# Revit family: AMZ 113_DN15-32_RFA
name_source: partatom
category: Pipe Accessories
units: mm (PartAtom-declared; Revit-internal decimal feet)

## family parameters
Always vertical = Yes
Cut with Voids When Loaded = No
OmniClass Number = 23.65.55.14.17
OmniClass Title = Adjusting/Controlling Valves for Liquid Services
Part Type = Valve - Breaks Into
Round Connector Dimension = Use Diameter
Shared = No
Work Plane-Based = No

## types (8) — shared parameters
082G1637 = AMZ Actuator_RFA : AMZ 112/113 Actuator_24V_082G1637
082G1638 = AMZ Actuator_RFA : AMZ 112/113 Actuator_230V_082G1638
Connection = Internal thread
Description = Motorized Control Valve
IfcExportAs = IfcValveType
IfcExportType = AMZ 113
LOD 200 = No
LOD 350 = Yes
Manufacturer = Danfoss
Max Medium Temperature = 130 °C
Max Operating Pressure = 6 bar
Min Medium Temperature = 2 °C
Nominal Flow (Text) = PN 40
Power = 4 VA
Power Consumption = 3.5 VA
URL = https://store.danfoss.com
Valve Body Material = Danfoss Copper Alloy

## per-type parameters (varying)
- AMZ 113_DN15_230V_082G5418: AMZ Actuator=AMZ Actuator_RFA : AMZ 112/113 Actuator_230V_082G1638; D=15 mm  [stored 0.0492126 ft]; H1=38 mm; H2=29 mm  [stored 0.0951444 ft]; HS=9 mm  [stored 0.0295276 ft]; Kvs=4.3 m³/h; L1=3.5 mm  [stored 0.0114829 ft]; LS=37 mm; Length=64.5 mm; Model=082G5418; Model Type=AMZ 113_DN15_230V; Power Supply=230 VAC; R1=11 mm  [stored 0.0360892 ft]; RN1=13.53 mm; RV1=13.53 mm; RV2=17 mm  [stored 0.0557743 ft]; RV3=9.06 mm; Voltage=230 V; W1=26.4 mm  [stored 0.0866142 ft]; W2=13.2 mm  [stored 0.0433071 ft]; W3=3.5 mm  [stored 0.0114829 ft]; W4=4 mm  [stored 0.0131234 ft]; WS1=18.5 mm  [stored 0.0606955 ft]; WS2=-18.5 mm  [stored -0.0606955 ft]; Weight=1.16 kg; connector diameter=27.06 mm; nut_depth1=5.75 mm  [stored 0.0188648 ft]; nut_depth2=6 mm  [stored 0.019685 ft]; nut_length=27.1 mm  [stored 0.0889108 ft]
- AMZ 113_DN20_230V_082G5419: AMZ Actuator=AMZ Actuator_RFA : AMZ 112/113 Actuator_230V_082G1638; D=20 mm  [stored 0.0656168 ft]; H1=42 mm; H2=33 mm; HS=9 mm  [stored 0.0295276 ft]; Kvs=8.3 m³/h; L1=3 mm  [stored 0.00984252 ft]; LS=37 mm; Length=76 mm; Model=082G5419; Model Type=AMZ 113_DN20_230V; Power Supply=230 VAC; R1=11 mm  [stored 0.0360892 ft]; RN1=17 mm  [stored 0.0557743 ft]; RV1=17.2 mm  [stored 0.0564304 ft]; RV2=21 mm  [stored 0.0688976 ft]; RV3=9.06 mm; Voltage=230 V; W1=28.5 mm  [stored 0.0935039 ft]; W2=17.2 mm  [stored 0.0564304 ft]; W3=3.5 mm  [stored 0.0114829 ft]; W4=4 mm  [stored 0.0131234 ft]; WS1=18.6 mm  [stored 0.0610236 ft]; WS2=-18.6 mm  [stored -0.0610236 ft]; Weight=1.42 kg; connector diameter=34 mm; nut_depth1=9.5 mm  [stored 0.031168 ft]; nut_depth2=9.5 mm  [stored 0.031168 ft]; nut_length=34 mm
- AMZ 113_DN25_230V_082G5420: AMZ Actuator=AMZ Actuator_RFA : AMZ 112/113 Actuator_230V_082G1638; D=25 mm  [stored 0.082021 ft]; H1=47 mm; H2=37.5 mm; HS=9.5 mm  [stored 0.031168 ft]; Kvs=13.0 m³/h; L1=3 mm  [stored 0.00984252 ft]; LS=42 mm; Length=97 mm; Model=082G5420; Model Type=AMZ 113_DN25_230V; Power Supply=230 VAC; R1=11.5 mm  [stored 0.0377297 ft]; RN1=22.19 mm; RV1=23 mm  [stored 0.0754593 ft]; RV2=26 mm; RV3=14 mm  [stored 0.0459318 ft]; Voltage=230 V; W1=35.5 mm; W2=20.1 mm  [stored 0.0659449 ft]; W3=3 mm  [stored 0.00984252 ft]; W4=6 mm  [stored 0.019685 ft]; WS1=21 mm  [stored 0.0688976 ft]; WS2=-21 mm  [stored -0.0688976 ft]; Weight=1.91 kg; connector diameter=44.38 mm; nut_depth1=12 mm  [stored 0.0393701 ft]; nut_depth2=12.5 mm  [stored 0.0410105 ft]; nut_length=44.38 mm
- AMZ 113_DN32_230V_082G5421: AMZ Actuator=AMZ Actuator_RFA : AMZ 112/113 Actuator_230V_082G1638; D=32 mm; H1=61.25 mm; H2=51.25 mm; HS=10 mm  [stored 0.0328084 ft]; Kvs=21.0 m³/h; L1=3 mm  [stored 0.00984252 ft]; LS=42 mm; Length=118 mm; Model=082G5421; Model Type=AMZ 113_DN32_230V; Power Supply=230 VAC; R1=11.5 mm  [stored 0.0377297 ft]; RN1=30 mm  [stored 0.0984252 ft]; RV1=28 mm  [stored 0.0918635 ft]; RV2=31 mm; RV3=15 mm  [stored 0.0492126 ft]; Voltage=230 V; W1=48 mm; W2=23.5 mm  [stored 0.0770997 ft]; W3=3 mm  [stored 0.00984252 ft]; W4=7.6 mm; WS1=21 mm  [stored 0.0688976 ft]; WS2=-21 mm  [stored -0.0688976 ft]; Weight=3.71 kg; connector diameter=60 mm; nut_depth1=11 mm  [stored 0.0360892 ft]; nut_depth2=11 mm  [stored 0.0360892 ft]; nut_length=60 mm
- AMZ 113_DN15_24V_082G5412: AMZ Actuator=AMZ Actuator_RFA : AMZ 112/113 Actuator_24V_082G1637; D=15 mm  [stored 0.0492126 ft]; H1=38 mm; H2=29 mm  [stored 0.0951444 ft]; HS=9 mm  [stored 0.0295276 ft]; Kvs=4.3 m³/h; L1=3.5 mm  [stored 0.0114829 ft]; LS=37 mm; Length=64.5 mm; Model=082G5412; Model Type=AMZ 113_DN15_24V; Power Supply=24 VAC; R1=11 mm  [stored 0.0360892 ft]; RN1=13.53 mm; RV1=13.53 mm; RV2=17 mm  [stored 0.0557743 ft]; RV3=9.06 mm; Voltage=24 V; W1=26.4 mm  [stored 0.0866142 ft]; W2=13.2 mm  [stored 0.0433071 ft]; W3=3.5 mm  [stored 0.0114829 ft]; W4=4 mm  [stored 0.0131234 ft]; WS1=18.5 mm  [stored 0.0606955 ft]; WS2=-18.5 mm  [stored -0.0606955 ft]; Weight=1.16 kg; connector diameter=27.06 mm; nut_depth1=5.75 mm  [stored 0.0188648 ft]; nut_depth2=6 mm  [stored 0.019685 ft]; nut_length=27.1 mm  [stored 0.0889108 ft]
- AMZ 113_DN20_24V_082G5413: AMZ Actuator=AMZ Actuator_RFA : AMZ 112/113 Actuator_24V_082G1637; D=20 mm  [stored 0.0656168 ft]; H1=42 mm; H2=33 mm; HS=9 mm  [stored 0.0295276 ft]; Kvs=8.3 m³/h; L1=3 mm  [stored 0.00984252 ft]; LS=37 mm; Length=76 mm; Model=082G5413; Model Type=AMZ 113_DN20_24V; Power Supply=24 VAC; R1=11 mm  [stored 0.0360892 ft]; RN1=17 mm  [stored 0.0557743 ft]; RV1=17.2 mm  [stored 0.0564304 ft]; RV2=21 mm  [stored 0.0688976 ft]; RV3=9.06 mm; Voltage=24 V; W1=28.5 mm  [stored 0.0935039 ft]; W2=17.2 mm  [stored 0.0564304 ft]; W3=3.5 mm  [stored 0.0114829 ft]; W4=4 mm  [stored 0.0131234 ft]; WS1=18.6 mm  [stored 0.0610236 ft]; WS2=-18.6 mm  [stored -0.0610236 ft]; Weight=1.42 kg; connector diameter=34 mm; nut_depth1=9.5 mm  [stored 0.031168 ft]; nut_depth2=9.5 mm  [stored 0.031168 ft]; nut_length=34 mm
- AMZ 113_DN25_24V_082G5414: AMZ Actuator=AMZ Actuator_RFA : AMZ 112/113 Actuator_24V_082G1637; D=25 mm  [stored 0.082021 ft]; H1=47 mm; H2=37.5 mm; HS=9.5 mm  [stored 0.031168 ft]; Kvs=13.0 m³/h; L1=3 mm  [stored 0.00984252 ft]; LS=42 mm; Length=97 mm; Model=082G5414; Model Type=AMZ 113_DN25_24V; Power Supply=24 VAC; R1=11.5 mm  [stored 0.0377297 ft]; RN1=22.19 mm; RV1=23 mm  [stored 0.0754593 ft]; RV2=26 mm; RV3=14 mm  [stored 0.0459318 ft]; Voltage=24 V; W1=35.5 mm; W2=20.1 mm  [stored 0.0659449 ft]; W3=3 mm  [stored 0.00984252 ft]; W4=6 mm  [stored 0.019685 ft]; WS1=21 mm  [stored 0.0688976 ft]; WS2=-21 mm  [stored -0.0688976 ft]; Weight=1.91 kg; connector diameter=44.38 mm; nut_depth1=12 mm  [stored 0.0393701 ft]; nut_depth2=12.5 mm  [stored 0.0410105 ft]; nut_length=44.38 mm
- AMZ 113_DN32_24V_082G5415: AMZ Actuator=AMZ Actuator_RFA : AMZ 112/113 Actuator_24V_082G1637; D=32 mm; H1=61.25 mm; H2=51.25 mm; HS=10 mm  [stored 0.0328084 ft]; Kvs=21.0 m³/h; L1=3 mm  [stored 0.00984252 ft]; LS=42 mm; Length=118 mm; Model=082G5415; Model Type=AMZ 113_DN32_24V; Power Supply=24 VAC; R1=11.5 mm  [stored 0.0377297 ft]; RN1=30 mm  [stored 0.0984252 ft]; RV1=28 mm  [stored 0.0918635 ft]; RV2=31 mm; RV3=15 mm  [stored 0.0492126 ft]; Voltage=24 V; W1=48 mm; W2=23.5 mm  [stored 0.0770997 ft]; W3=3 mm  [stored 0.00984252 ft]; W4=7.6 mm; WS1=21 mm  [stored 0.0688976 ft]; WS2=-21 mm  [stored -0.0688976 ft]; Weight=3.71 kg; connector diameter=60 mm; nut_depth1=11 mm  [stored 0.0360892 ft]; nut_depth2=11 mm  [stored 0.0360892 ft]; nut_length=60 mm

note: [stored X ft] marks values corroborated as IEEE doubles in the binary element streams (Revit-internal decimal feet)

## geometry (parser evidence)
native form markers: Sweep x3
no freeform markers — native parametric forms only
